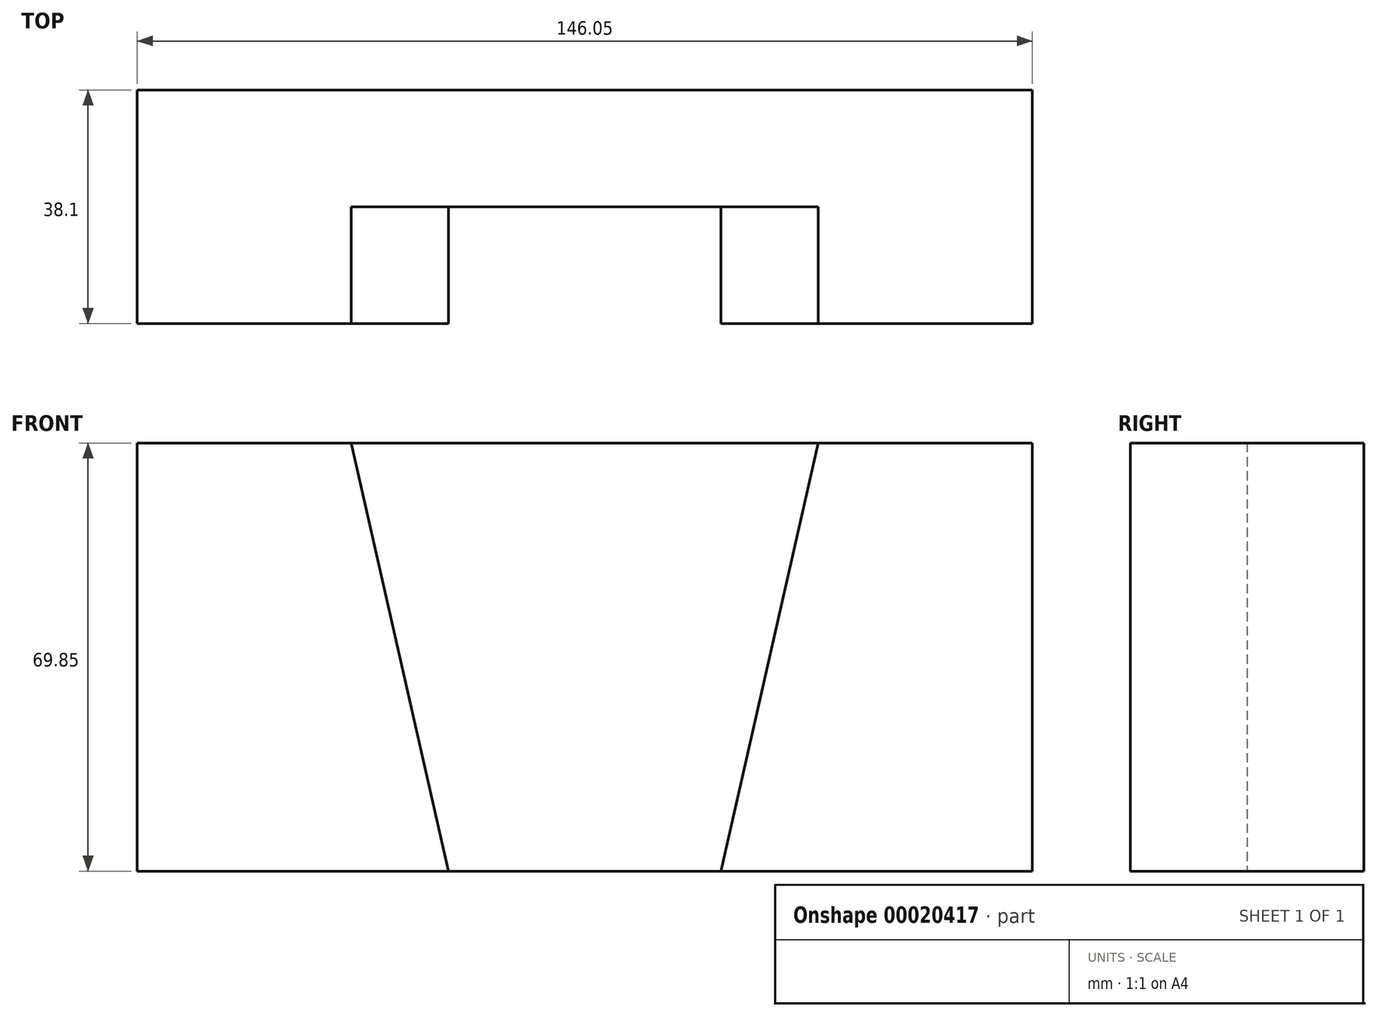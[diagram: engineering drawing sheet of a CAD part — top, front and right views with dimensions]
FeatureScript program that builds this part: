
annotation { "Feature Type Name" : "Feature", "Feature Type Description" : "" }
export const myFeature = defineFeature(function(context is Context, id is Id, definition is map)
    precondition{}
    {
        {
            var Q0;
            Q0=qCreatedBy(makeId("Front.planeOp"),FACE);
            var sketch = newSketch(context, id + "F0", { "sketchPlane" : qUnion([Q0])});
            skLineSegment(sketch, "E0", {"start": v(-74.8, 43.19) * mm, "end": v(71.24, 43.19) * mm});
            skLineSegment(sketch, "E1", {"start": v(71.24, 43.19) * mm, "end": v(71.24, -26.66) * mm});
            skLineSegment(sketch, "E2", {"start": v(71.24, -26.66) * mm, "end": v(-74.8, -26.66) * mm});
            skLineSegment(sketch, "E3", {"start": v(-74.8, -26.66) * mm, "end": v(-74.8, 43.19) * mm});
            skLineSegment(sketch, "E4", {"start": v(-39.88, 43.19) * mm, "end": v(-24, -26.66) * mm});
            skLineSegment(sketch, "E5", {"start": v(20.44, -26.66) * mm, "end": v(36.32, 43.19) * mm});
            skSolve(sketch);
        }
        {
            var Q0;
            Q0 = qSketchRegion(id + "F0", true);
            extrude(context, id + "F1", {"entities" : qUnion([Q0]), "depth" : 19.05 * mm});
        }
        {
            var Q0;
            {var subQ2=sQuery(id+"F0.wireOp",EDGE,"E3");Q0=makeQuery(id+"F0.imprint","IMPRINT",FACE,{"disambiguationData":[TD([[makeQuery(id+"F0.imprint","IMPRINT",EDGE,{"derivedFrom":subQ2}),-1.0]])]});}
            var Q1;
            {var subQ2=sQuery(id+"F0.wireOp",EDGE,"E1");Q1=makeQuery(id+"F0.imprint","IMPRINT",FACE,{"disambiguationData":[TD([[makeQuery(id+"F0.imprint","IMPRINT",EDGE,{"derivedFrom":subQ2}),-1.0]])]});}
            extrude(context, id + "F2", {"entities" : qUnion([Q0, Q1]), "operationType" : NewBodyOperationType.ADD, "depth" : 38.1 * mm});
        }
    });
